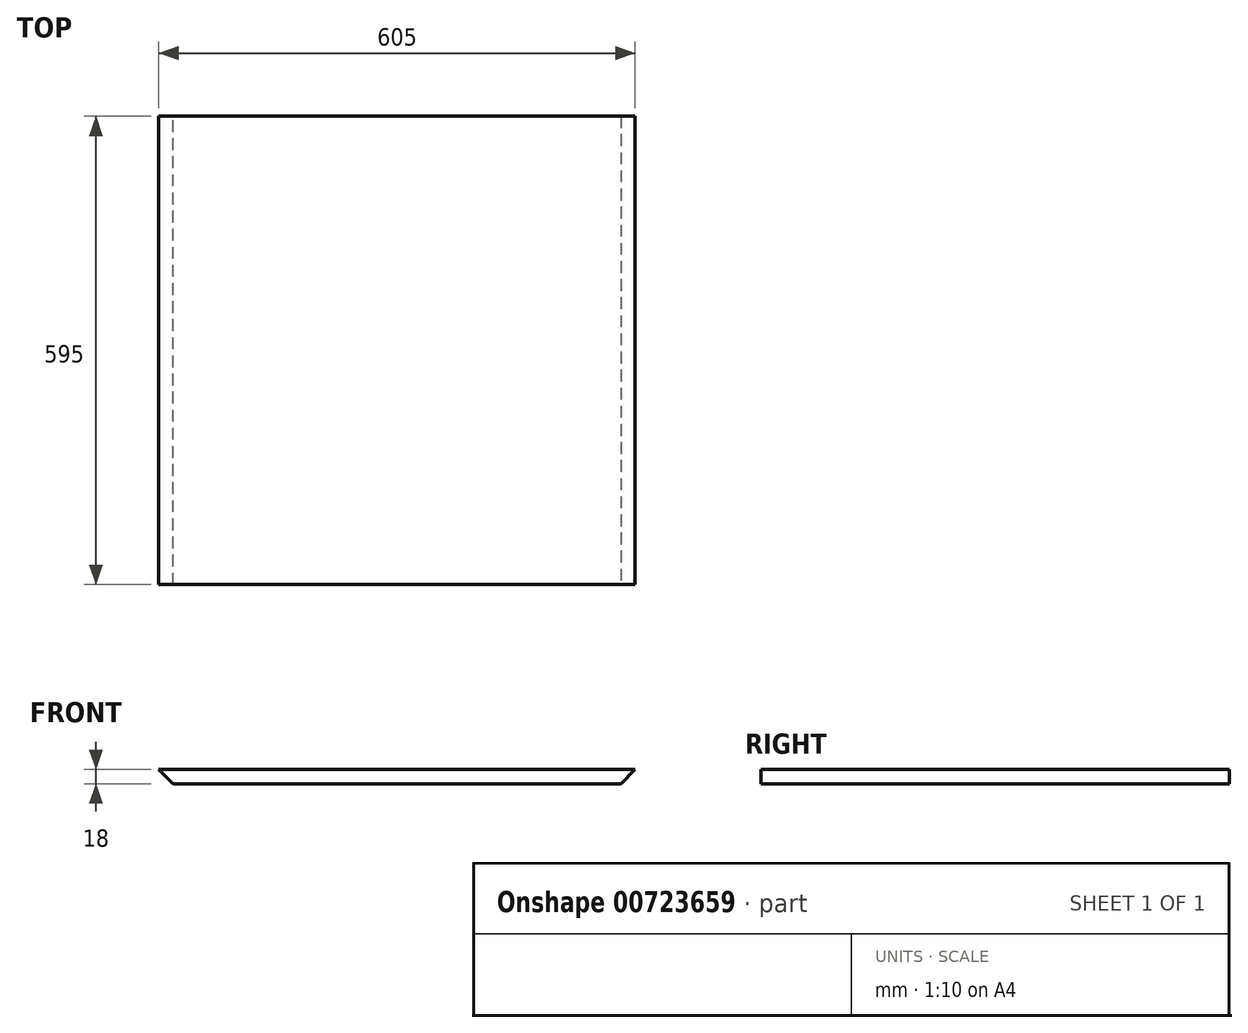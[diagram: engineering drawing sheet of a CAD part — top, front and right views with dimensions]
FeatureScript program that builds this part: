
annotation { "Feature Type Name" : "Feature", "Feature Type Description" : "" }
export const myFeature = defineFeature(function(context is Context, id is Id, definition is map)
    precondition{}
    {
        {
            var Q0;
            Q0=qCreatedBy(makeId("Top.planeOp"),FACE);
            var sketch = newSketch(context, id + "F0", { "sketchPlane" : qUnion([Q0])});
            skLineSegment(sketch, "E0.bottom", {"start": v(-300.4, 328.21) * mm, "end": v(304.6, 328.21) * mm});
            skLineSegment(sketch, "E0.top", {"start": v(-300.4, -266.79) * mm, "end": v(304.6, -266.79) * mm});
            skLineSegment(sketch, "E0.left", {"start": v(-300.4, 328.21) * mm, "end": v(-300.4, -266.79) * mm});
            skLineSegment(sketch, "E0.right", {"start": v(304.6, 328.21) * mm, "end": v(304.6, -266.79) * mm});
            skSolve(sketch);
        }
        {
            var Q0;
            Q0 = qSketchRegion(id + "F0", true);
            extrude(context, id + "F1", {"entities" : qUnion([Q0]), "oppositeDirection" : true, "depth" : 18 * mm, "offsetDistance" : 25 * mm});
        }
        {
            var Q0;
            Q0=makeQuery(id+"F1.opExtrude","CAP_EDGE",EDGE,{"disambiguationData":[OSD([sQuery(id+"F0.wireOp",EDGE,"E0.left")])],"isStart":false});
            var Q1;
            Q1=makeQuery(id+"F1.opExtrude","CAP_EDGE",EDGE,{"disambiguationData":[OSD([sQuery(id+"F0.wireOp",EDGE,"E0.right")])],"isStart":false});
            chamfer(context, id + "F2", {"entities" : qUnion([Q0, Q1]), "width" : 18 * mm, "tangentPropagation" : true});
        }
    });
